# Revit family: Drain_Floor_Round_Zurn-1735
name_source: partatom
category: Plumbing Fixtures
units: mm (PartAtom-declared; Revit-internal decimal feet)

## family parameters
Always vertical = Yes
Cut with Voids When Loaded = No
Maintain Annotation Orientation = No
OmniClass Number = 23.70.50.21.24.14
OmniClass Title = Deck Waste Water Drains
Part Type = Normal
Room Calculation Point = No
Round Connector Dimension = Use Radius
Shared = No
Work Plane-Based = No

## types (12) — shared parameters
Assembly Code = D2030300
CW Connection = No
Default Elevation = 10 "
Description = 12 [305] DIAMETER FLOOR DRAIN
Grate Open Area(Sq.In) = 33 in²
HW Connection = No
Manufacturer = Zurn Water, LLC
Manufacurer Brand = Zurn
Modified Date = 11/03/2025
Product Documentation Link = https://files.zurn.com
Product Page URL = https://www.zurn.com
Product data url = https://www.bimobject.com
URL = www.zurn.com
Vent Connection = No
WFU = 1
Waste Connection = Yes
zero-valued in all types: CWFU, HWFU

## per-type parameters (varying)
| type | 'E' Body Height | Approx. Weight (Lbs) | Main Material | Model | Pipe Size "A"(Inner Radius) | Pipe Size "A"(Outer Radius) | Pipe Size 'A' (Inner Diameter) | Pipe Size 'A' (Nominal Diameter) | Pipe Size 'A' (Nominal Radius) | Pipe Size 'A' (Outer Diameter) | Type Comments |
| Z1735-3BW | 6 " | 50 " | Steel - Zurn - Stainless - Type - 304 | Z1735 | 1.534 " | 1.75 " | 3.068 " | 3 " | 1.5 " | 3.5 " | Z1735 3 Inch Butt-weld Outlet |
| Z1735-4BW | 6 " | 50 " | Steel - Zurn - Stainless - Type - 304 | Z1735 | 2.013 " | 2.25 " | 4.026 " | 4 " | 2 " | 4.5 " | Z1735 4 Inch Butt-weld Outlet |
| Z1735-6BW | 6 " | 54 " | Steel - Zurn - Stainless - Type - 304 | Z1735 | 3.033 " | 3.313 " | 6.065 " | 6 " | 3 " | 6.625 " | Z1735 6 Inch Butt-weld Outlet |
| Z1735-3IP | 5.25 " | 50 " | Steel - Zurn - Stainless - Type - 304 | Z1735 | 1.534 " | 1.75 " | 3.068 " | 3 " | 1.5 " | 3.5 " | Z1735 3 Inch Threaded Outlet |
| Z1735-4IP | 5.25 " | 50 " | Steel - Zurn - Stainless - Type - 304 | Z1735 | 2.013 " | 2.25 " | 4.026 " | 4 " | 2 " | 4.5 " | Z1735 4 Inch Threaded Outlet |
| Z1735-6IP | 5.25 " | 54 " | Steel - Zurn - Stainless - Type - 304 | Z1735 | 3.033 " | 3.313 " | 6.065 " | 6 " | 3 " | 6.625 " | Z1735 6 Inch Threaded Outlet |
| ZM1735-3BW | 6 " | 50 " | Steel - Zurn - Stainless - Type - 316 | ZM1735 | 1.534 " | 1.75 " | 3.068 " | 3 " | 1.5 " | 3.5 " | ZM1735 3 Inch Butt-weld Outlet |
| ZM1735-4BW | 6 " | 50 " | Steel - Zurn - Stainless - Type - 316 | ZM1735 | 2.013 " | 2.25 " | 4.026 " | 4 " | 2 " | 4.5 " | ZM1735 4 Inch Butt-weld Outlet |
| ZM1735-6BW | 6 " | 54 " | Steel - Zurn - Stainless - Type - 316 | ZM1735 | 3.033 " | 3.313 " | 6.065 " | 6 " | 3 " | 6.625 " | ZM1735 6 Inch Butt-weld Outlet |
| ZM1735-3IP | 5.25 " | 50 " | Steel - Zurn - Stainless - Type - 316 | ZM1735 | 1.534 " | 1.75 " | 3.068 " | 3 " | 1.5 " | 3.5 " | ZM1735 3 Inch Threaded Outlet |
| ZM1735-4IP | 5.25 " | 50 " | Steel - Zurn - Stainless - Type - 316 | ZM1735 | 2.013 " | 2.25 " | 4.026 " | 4 " | 2 " | 4.5 " | ZM1735 4 Inch Threaded Outlet |
| ZM1735-6IP | 5.25 " | 54 " | Steel - Zurn - Stainless - Type - 316 | ZM1735 | 3.033 " | 3.313 " | 6.065 " | 6 " | 3 " | 6.625 " | ZM1735 6 Inch Threaded Outlet |

## geometry (parser evidence)
native form markers: Sweep x5
no freeform markers — native parametric forms only
